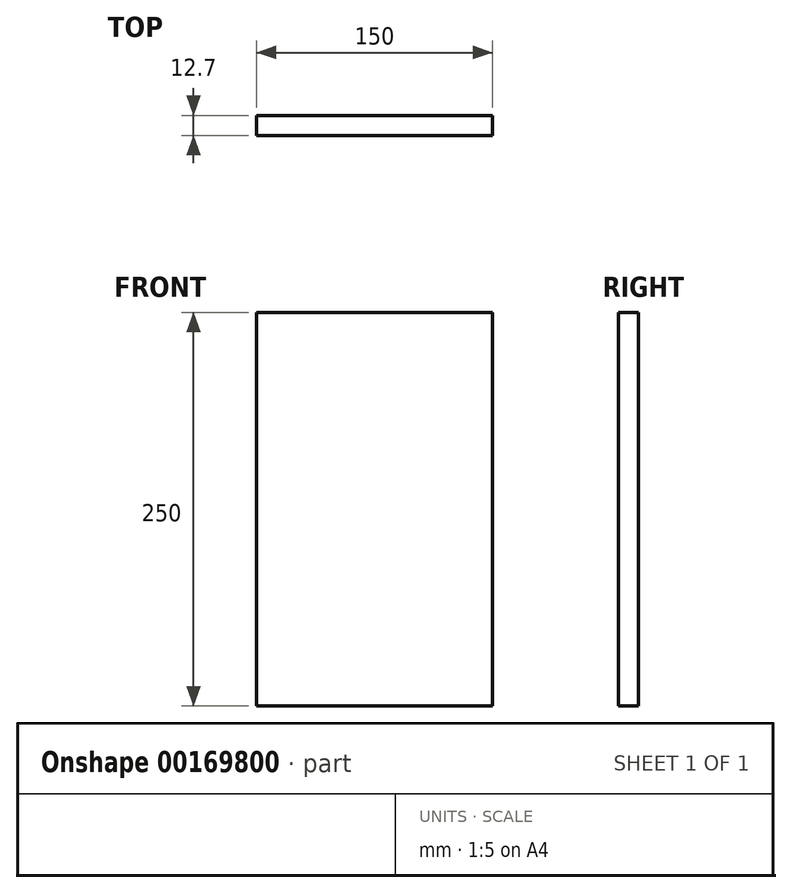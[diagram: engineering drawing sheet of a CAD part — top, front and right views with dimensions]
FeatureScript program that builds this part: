
annotation { "Feature Type Name" : "Feature", "Feature Type Description" : "" }
export const myFeature = defineFeature(function(context is Context, id is Id, definition is map)
    precondition{}
    {
        {
            var Q0;
            Q0=qCreatedBy(makeId("Front.planeOp"),FACE);
            var sketch = newSketch(context, id + "F0", { "sketchPlane" : qUnion([Q0])});
            skLineSegment(sketch, "E0.bottom", {"start": v(-75, -125) * mm, "end": v(75, -125) * mm});
            skLineSegment(sketch, "E0.top", {"start": v(-75, 125) * mm, "end": v(75, 125) * mm});
            skLineSegment(sketch, "E0.left", {"start": v(-75, -125) * mm, "end": v(-75, 125) * mm});
            skLineSegment(sketch, "E0.right", {"start": v(75, -125) * mm, "end": v(75, 125) * mm});
            skPoint(sketch, "E0.middle", {"position": v(0, 0) * mm});
            skSolve(sketch);
        }
        {
            var Q0;
            Q0=qSketchRegion(id+"F0",true);
            extrude(context, id + "F1", {"entities" : qUnion([Q0]), "depth" : 25.4 / 2 * mm});
        }
    });
